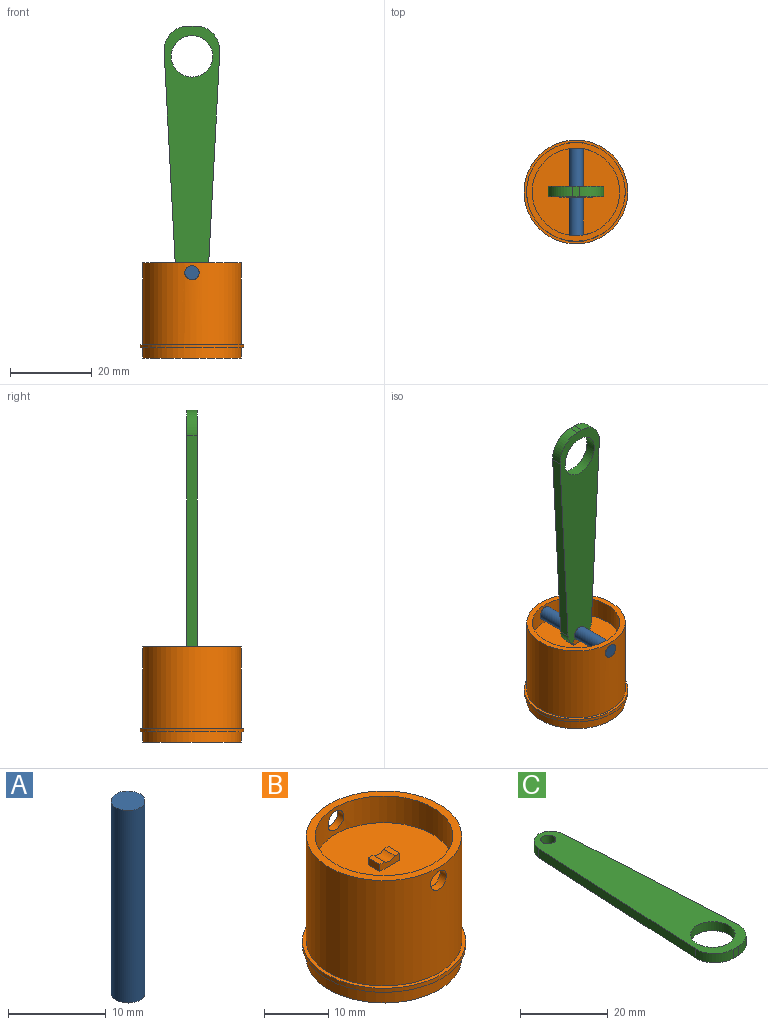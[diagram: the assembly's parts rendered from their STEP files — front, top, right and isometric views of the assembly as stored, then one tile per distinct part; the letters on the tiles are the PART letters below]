
ASSEMBLY  parts=3 mates=2
PART A: 3 faces, bbox 3.5x3.5x24.1 mm
  f0: cylinder r=1.74mm len=24.13mm, axis (0,0,-1), area 263.8mm2, adj f1,f2
  f1: plane 3.48x3.48mm, normal (0,0,1), area 9.5mm2, adj f0
  f2: plane 3.48x3.48mm, normal (0,0,-1), area 9.5mm2, adj f0
PART B: 18 faces, bbox 25.4x25.4x23.3 mm
  f0: cylinder r=12.06mm len=24.13mm, axis (0,0,-1), area 1500.1mm2, adj f7,f9,f16,f17
  f1: cylinder r=10.71mm len=21.42mm, axis (0,0,1), area 322.7mm2, adj f9,f10,f16,f17
  f2: plane 2.54x1.03mm, normal (0,0,1), area 2.6mm2, adj f11,f12,f14,f15
  f3: plane 2.54x1.03mm, normal (0,0,1), area 2.6mm2, adj f12,f13,f14,f15
  f4: cylinder r=12.06mm len=24.13mm, axis (0,0,-1), area 188.8mm2, adj f5,f8
  f5: plane 24.13x24.13mm, normal (0,0,-1), area 457.3mm2, adj f4
  f6: cylinder r=12.7mm len=25.4mm, axis (0,0,-1), area 60.8mm2, adj f7,f8
  f7: plane 25.4x25.4mm, normal (0,0,1), area 49.4mm2, adj f0,f6
  f8: plane 25.4x25.4mm, normal (0,0,-1), area 49.4mm2, adj f4,f6
  f9: plane 24.13x24.13mm, normal (0,0,1), area 97mm2, adj f0,f1
  f10: plane 21.42x21.42mm, normal (0,0,1), area 349.1mm2, adj f1,f11,f12,f13,f14
  f11: plane 2.54x1.33mm, normal (-1,0,0), area 3.4mm2, adj f2,f10,f12,f14
  f12: plane 4.39x1.33mm, normal (0,-1,0), area 5.1mm2, adj f2,f3,f10,f11,f13,f15
  f13: plane 2.54x1.33mm, normal (1,0,0), area 3.4mm2, adj f3,f10,f12,f14
  f14: plane 4.39x1.33mm, normal (0,1,0), area 5.1mm2, adj f2,f3,f10,f11,f13,f15
  f15: cylinder r=1.75mm len=2.54mm, axis (0,-1,0), area 6.5mm2, adj f2,f3,f12,f14
  f16: cylinder r=1.75mm len=3.49mm, axis (0,-1,0), area 15mm2, adj f0,f1
  f17: cylinder r=1.75mm len=3.49mm, axis (0,-1,0), area 15mm2, adj f0,f1
PART C: 11 faces, bbox 13.6x63.5x2.5 mm
  f0: plane 53.05x2.78mm, normal (-1,0.05,0), area 134.9mm2, adj f3,f4,f6,f7
  f1: plane 2.54x1.64mm, normal (0,-1,0), area 4.2mm2, adj f3,f4,f7,f8
  f2: plane 53.05x2.78mm, normal (1,0.05,0), area 134.9mm2, adj f3,f4,f5,f8
  f3: plane 63.49x13.63mm, normal (0,0,1), area 580mm2, adj f0,f1,f2,f5,f6,f7,f8,f9
  f4: plane 63.49x13.63mm, normal (0,0,-1), area 580mm2, adj f0,f1,f2,f5,f6,f7,f8,f9
  f5: cylinder r=4.37mm len=4.13mm, axis (0,0,-1), area 16mm2, adj f2,f3,f4,f6
  f6: cylinder r=4.37mm len=4.13mm, axis (0,0,-1), area 16mm2, adj f0,f3,f4,f5
  f7: cylinder r=5.99mm len=6.31mm, axis (0,0,1), area 24.7mm2, adj f0,f1,f3,f4
  f8: cylinder r=5.99mm len=6.31mm, axis (0,0,1), area 24.7mm2, adj f1,f2,f3,f4
  f9: cylinder r=5.08mm len=10.16mm, axis (0,0,1), area 81.1mm2, adj f3,f4
  f10: cylinder r=1.74mm len=3.48mm, axis (0,0,1), area 27.8mm2, adj f3,f4
PLACE A rot(axis=(-1,0,0),90deg) t=(-2.34,-1.58,33.99)mm
PLACE B t=(-2.34,10.47,13.14)mm
PLACE C rot(axis=(-1,0,0),90deg) t=(1.47,9.21,68.18)mm
MATE revolute A.f0 <-> C.f10  axis (0,-1,0) through (-2.34,10.48,33.99)mm
MATE revolute A.f0 <-> B.f15  axis (0,-1,0) through (-2.34,22.55,33.99)mm
